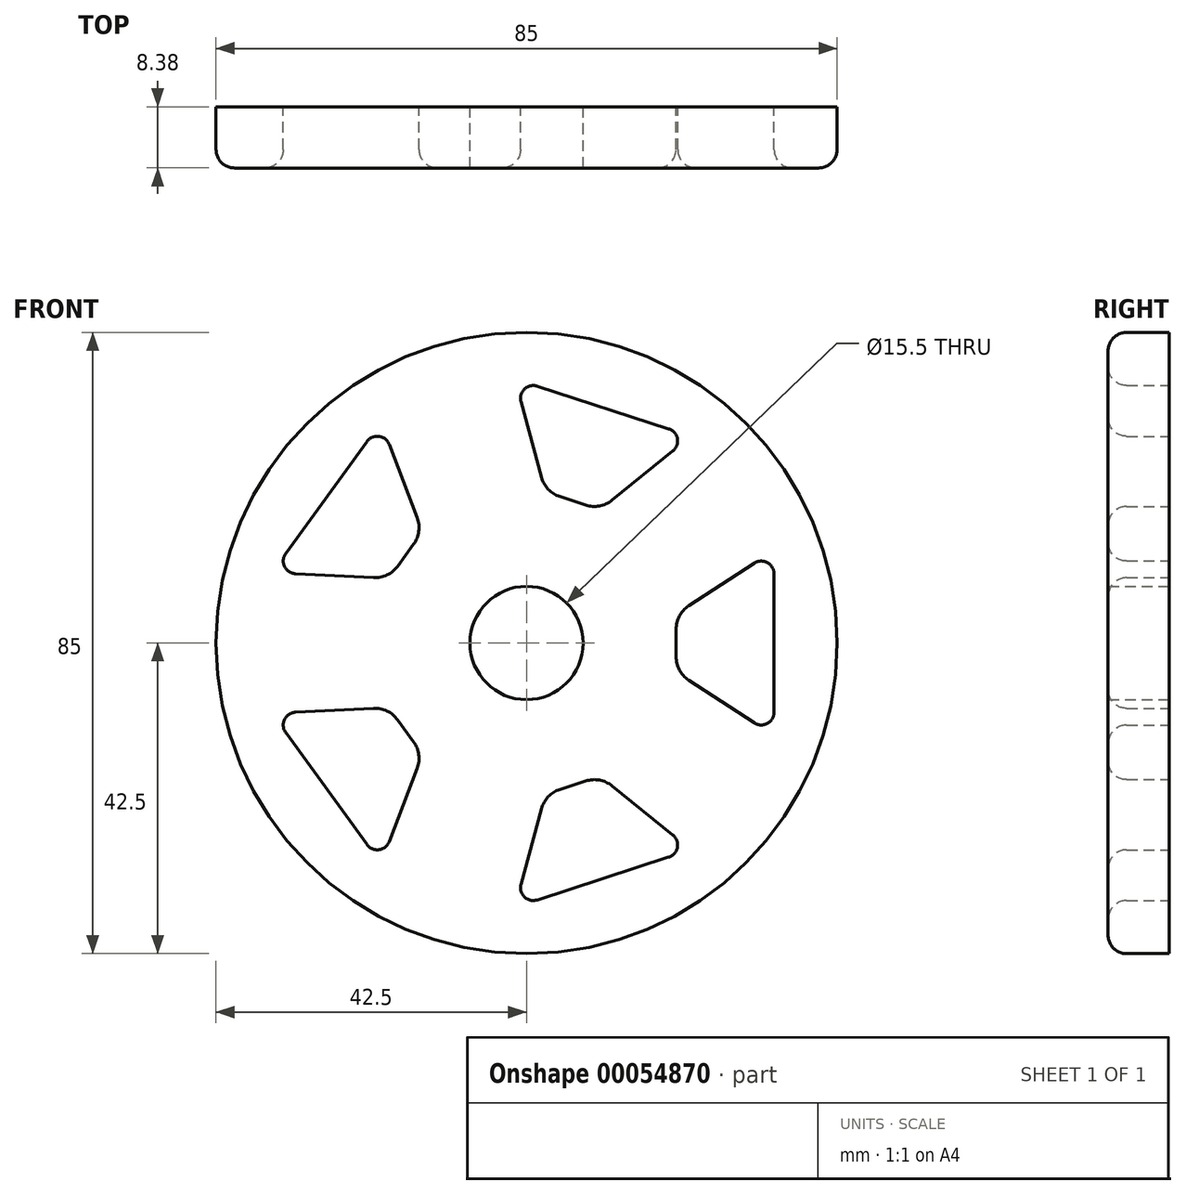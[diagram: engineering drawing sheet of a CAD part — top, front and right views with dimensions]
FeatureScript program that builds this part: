
annotation { "Feature Type Name" : "Feature", "Feature Type Description" : "" }
export const myFeature = defineFeature(function(context is Context, id is Id, definition is map)
    precondition{}
    {
        {
            var Q0;
            Q0=qCreatedBy(makeId("Front.planeOp"),FACE);
            var sketch = newSketch(context, id + "F0", { "sketchPlane" : qUnion([Q0])});
            skCircle(sketch, "E0", {"center": v(0, 0) * mm, "radius": 42.5 * mm});
            skCircle(sketch, "E1", {"center": v(0, 0) * mm, "radius": 7.75 * mm});
            skLineSegment(sketch, "E2", {"start": v(20.46, 1.88) * mm, "end": v(20.46, 0) * mm});
            skLineSegment(sketch, "E3", {"start": v(22.19, 5.07) * mm, "end": v(31.17, 10.93) * mm});
            skLineSegment(sketch, "E4", {"start": v(33.88, 9.46) * mm, "end": v(33.88, 0) * mm});
            skPoint(sketch, "E5.visualSharp", {"position": v(20.46, 3.94) * mm});
            skArc(sketch, "E5.filletArc", {"start": v(22.19, 5.07) * mm, "mid": v(20.92, 3.69) * mm, "end": v(20.46, 1.88) * mm});
            skPoint(sketch, "E6.visualSharp", {"position": v(33.88, 12.7) * mm});
            skArc(sketch, "E6.filletArc", {"start": v(33.88, 9.46) * mm, "mid": v(32.96, 11) * mm, "end": v(31.17, 10.93) * mm});
            skLineSegment(sketch, "E7.MirrorCS", {"start": v(33.88, -9.46) * mm, "end": v(33.88, 0) * mm});
            skArc(sketch, "E8.MirrorCS", {"start": v(33.88, -9.46) * mm, "mid": v(32.96, -11) * mm, "end": v(31.17, -10.93) * mm});
            skLineSegment(sketch, "E9.MirrorCS", {"start": v(20.46, -1.88) * mm, "end": v(20.46, 0) * mm});
            skArc(sketch, "E10.MirrorCS", {"start": v(22.19, -5.07) * mm, "mid": v(20.92, -3.69) * mm, "end": v(20.46, -1.88) * mm});
            skLineSegment(sketch, "E11.MirrorCS", {"start": v(22.19, -5.07) * mm, "end": v(31.17, -10.93) * mm});
            skLineSegment(sketch, "E12.1.0", {"start": v(2.04, 22.67) * mm, "end": v(-0.76, 33.02) * mm});
            skArc(sketch, "E12.1.1", {"start": v(1.47, 35.15) * mm, "mid": v(-0.28, 34.75) * mm, "end": v(-0.76, 33.02) * mm});
            skLineSegment(sketch, "E12.1.2", {"start": v(1.47, 35.15) * mm, "end": v(10.47, 32.22) * mm});
            skLineSegment(sketch, "E12.1.3", {"start": v(19.47, 29.3) * mm, "end": v(10.47, 32.22) * mm});
            skArc(sketch, "E12.1.4", {"start": v(19.47, 29.3) * mm, "mid": v(20.65, 27.95) * mm, "end": v(20.03, 26.26) * mm});
            skLineSegment(sketch, "E12.1.5", {"start": v(11.67, 19.54) * mm, "end": v(20.03, 26.26) * mm});
            skArc(sketch, "E12.1.6", {"start": v(11.67, 19.54) * mm, "mid": v(9.97, 18.76) * mm, "end": v(8.1, 18.88) * mm});
            skLineSegment(sketch, "E12.1.7", {"start": v(8.1, 18.88) * mm, "end": v(6.32, 19.46) * mm});
            skLineSegment(sketch, "E12.1.8", {"start": v(4.54, 20.04) * mm, "end": v(6.32, 19.46) * mm});
            skArc(sketch, "E12.1.9", {"start": v(2.04, 22.67) * mm, "mid": v(2.96, 21.04) * mm, "end": v(4.54, 20.04) * mm});
            skLineSegment(sketch, "E12.2.0", {"start": v(-20.93, 8.94) * mm, "end": v(-31.64, 9.48) * mm});
            skArc(sketch, "E12.2.1", {"start": v(-32.97, 12.26) * mm, "mid": v(-33.13, 10.47) * mm, "end": v(-31.64, 9.48) * mm});
            skLineSegment(sketch, "E12.2.2", {"start": v(-32.97, 12.26) * mm, "end": v(-27.41, 19.91) * mm});
            skLineSegment(sketch, "E12.2.3", {"start": v(-21.85, 27.57) * mm, "end": v(-27.41, 19.91) * mm});
            skArc(sketch, "E12.2.4", {"start": v(-21.85, 27.57) * mm, "mid": v(-20.2, 28.28) * mm, "end": v(-18.8, 27.16) * mm});
            skLineSegment(sketch, "E12.2.5", {"start": v(-14.97, 17.14) * mm, "end": v(-18.8, 27.16) * mm});
            skArc(sketch, "E12.2.6", {"start": v(-14.97, 17.14) * mm, "mid": v(-14.76, 15.28) * mm, "end": v(-15.45, 13.55) * mm});
            skLineSegment(sketch, "E12.2.7", {"start": v(-15.45, 13.55) * mm, "end": v(-16.55, 12.03) * mm});
            skLineSegment(sketch, "E12.2.8", {"start": v(-17.66, 10.5) * mm, "end": v(-16.55, 12.03) * mm});
            skArc(sketch, "E12.2.9", {"start": v(-20.93, 8.94) * mm, "mid": v(-19.1, 9.31) * mm, "end": v(-17.66, 10.5) * mm});
            skLineSegment(sketch, "E12.3.0", {"start": v(-14.97, -17.14) * mm, "end": v(-18.8, -27.16) * mm});
            skArc(sketch, "E12.3.1", {"start": v(-21.85, -27.57) * mm, "mid": v(-20.2, -28.28) * mm, "end": v(-18.8, -27.16) * mm});
            skLineSegment(sketch, "E12.3.2", {"start": v(-21.85, -27.57) * mm, "end": v(-27.41, -19.91) * mm});
            skLineSegment(sketch, "E12.3.3", {"start": v(-32.97, -12.26) * mm, "end": v(-27.41, -19.91) * mm});
            skArc(sketch, "E12.3.4", {"start": v(-32.97, -12.26) * mm, "mid": v(-33.13, -10.47) * mm, "end": v(-31.64, -9.48) * mm});
            skLineSegment(sketch, "E12.3.5", {"start": v(-20.93, -8.94) * mm, "end": v(-31.64, -9.48) * mm});
            skArc(sketch, "E12.3.6", {"start": v(-20.93, -8.94) * mm, "mid": v(-19.1, -9.31) * mm, "end": v(-17.66, -10.5) * mm});
            skLineSegment(sketch, "E12.3.7", {"start": v(-17.66, -10.5) * mm, "end": v(-16.55, -12.03) * mm});
            skLineSegment(sketch, "E12.3.8", {"start": v(-15.45, -13.55) * mm, "end": v(-16.55, -12.03) * mm});
            skArc(sketch, "E12.3.9", {"start": v(-14.97, -17.14) * mm, "mid": v(-14.76, -15.28) * mm, "end": v(-15.45, -13.55) * mm});
            skLineSegment(sketch, "E12.4.0", {"start": v(11.67, -19.54) * mm, "end": v(20.03, -26.26) * mm});
            skArc(sketch, "E12.4.1", {"start": v(19.47, -29.3) * mm, "mid": v(20.65, -27.95) * mm, "end": v(20.03, -26.26) * mm});
            skLineSegment(sketch, "E12.4.2", {"start": v(19.47, -29.3) * mm, "end": v(10.47, -32.22) * mm});
            skLineSegment(sketch, "E12.4.3", {"start": v(1.47, -35.15) * mm, "end": v(10.47, -32.22) * mm});
            skArc(sketch, "E12.4.4", {"start": v(1.47, -35.15) * mm, "mid": v(-0.28, -34.75) * mm, "end": v(-0.76, -33.02) * mm});
            skLineSegment(sketch, "E12.4.5", {"start": v(2.04, -22.67) * mm, "end": v(-0.76, -33.02) * mm});
            skArc(sketch, "E12.4.6", {"start": v(2.04, -22.67) * mm, "mid": v(2.96, -21.04) * mm, "end": v(4.54, -20.04) * mm});
            skLineSegment(sketch, "E12.4.7", {"start": v(4.54, -20.04) * mm, "end": v(6.32, -19.46) * mm});
            skLineSegment(sketch, "E12.4.8", {"start": v(8.1, -18.88) * mm, "end": v(6.32, -19.46) * mm});
            skArc(sketch, "E12.4.9", {"start": v(11.67, -19.54) * mm, "mid": v(9.97, -18.76) * mm, "end": v(8.1, -18.88) * mm});
            skSolve(sketch);
        }
        {
            var Q0;
            Q0 = qSketchRegion(id + "F0", true);
            extrude(context, id + "F1", {"entities" : qUnion([Q0]), "depth" : 8.38 * mm});
        }
        {
            var Q0;
            Q0=makeQuery(id+"F1.opExtrude","CAP_EDGE",EDGE,{"disambiguationData":[OSD([sQuery(id+"F0.wireOp",EDGE,"E3")])],"isStart":false});
            var Q1;
            Q1=makeQuery(id+"F1.opExtrude","CAP_EDGE",EDGE,{"disambiguationData":[OSD([sQuery(id+"F0.wireOp",EDGE,"E12.1.7"),sQuery(id+"F0.wireOp",EDGE,"E12.1.8")])],"isStart":false});
            var Q2;
            Q2=makeQuery(id+"F1.opExtrude","CAP_EDGE",EDGE,{"disambiguationData":[OSD([sQuery(id+"F0.wireOp",EDGE,"E12.2.7"),sQuery(id+"F0.wireOp",EDGE,"E12.2.8")])],"isStart":false});
            var Q3;
            Q3=makeQuery(id+"F1.opExtrude","CAP_EDGE",EDGE,{"disambiguationData":[OSD([sQuery(id+"F0.wireOp",EDGE,"E12.3.7"),sQuery(id+"F0.wireOp",EDGE,"E12.3.8")])],"isStart":false});
            var Q4;
            Q4=makeQuery(id+"F1.opExtrude","CAP_EDGE",EDGE,{"disambiguationData":[OSD([sQuery(id+"F0.wireOp",EDGE,"E12.4.7"),sQuery(id+"F0.wireOp",EDGE,"E12.4.8")])],"isStart":false});
            var Q5;
            Q5=makeQuery(id+"F1.opExtrude","CAP_EDGE",EDGE,{"disambiguationData":[OSD([sQuery(id+"F0.wireOp",EDGE,"E0")])],"isStart":false});
            fillet(context, id + "F2", {"entities" : qUnion([Q0, Q1, Q2, Q3, Q4, Q5]), "radius" : 2.54 * mm, "tangentPropagation" : true, "allowEdgeOverflow" : false});
        }
    });
